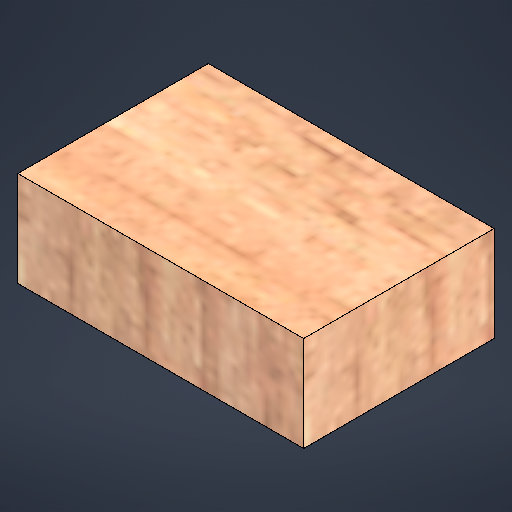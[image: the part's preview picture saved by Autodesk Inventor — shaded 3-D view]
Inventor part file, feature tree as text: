
AUTODESK INVENTOR PART (.ipt)
format: ipt  version: 2025.3 (Build 293356000, 356)  size: 347,136 bytes
history: native  units: mm
features: extrude x1, sketch x1
ambient origin geometry x8: Origin, YZ Plane, XZ Plane, XY Plane, X Axis, Y Axis, Z Axis, Center Point
bodies: Solid1 (feature_tree)
feature tree (2):
  extrude  "Extrusion1"  Depth=30.0mm
  sketch  "Sketch1"  dims[d0=45.0mm d1=30.0mm d2=15.0mm d3=0.0mm]
